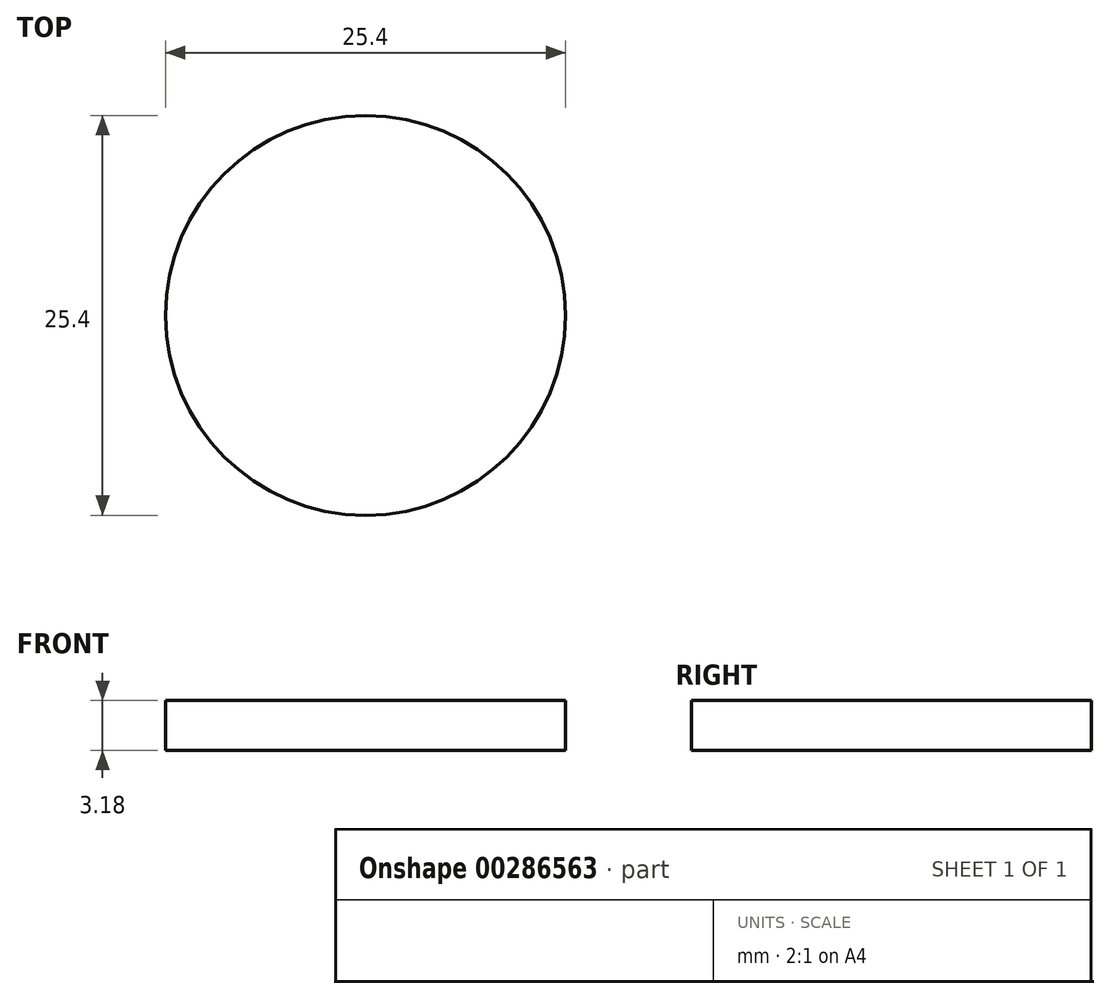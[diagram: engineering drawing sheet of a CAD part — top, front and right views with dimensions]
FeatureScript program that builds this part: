
annotation { "Feature Type Name" : "Feature", "Feature Type Description" : "" }
export const myFeature = defineFeature(function(context is Context, id is Id, definition is map)
    precondition{}
    {
        {
            var Q0;
            Q0=qCreatedBy(makeId("Top.planeOp"),FACE);
            var sketch = newSketch(context, id + "F0", { "sketchPlane" : qUnion([Q0])});
            skCircle(sketch, "E0", {"center": v(0, 0) * mm, "radius": 12.7 * mm});
            skSolve(sketch);
        }
        {
            var Q0;
            Q0=qSketchRegion(id+"F0",true);
            var Q1;
            Q1=makeQuery(id+"F0.imprint","IMPRINT",FACE,{"disambiguationData":[TD([[makeQuery(id+"F0.imprint","IMPRINT",EDGE,{"derivedFrom":sQuery(id+"F0.wireOp",EDGE,"E0")}),1.0]])]});
            extrude(context, id + "F1", {"entities" : qUnion([Q0, Q1]), "depth" : 3.17 * mm});
        }
    });
